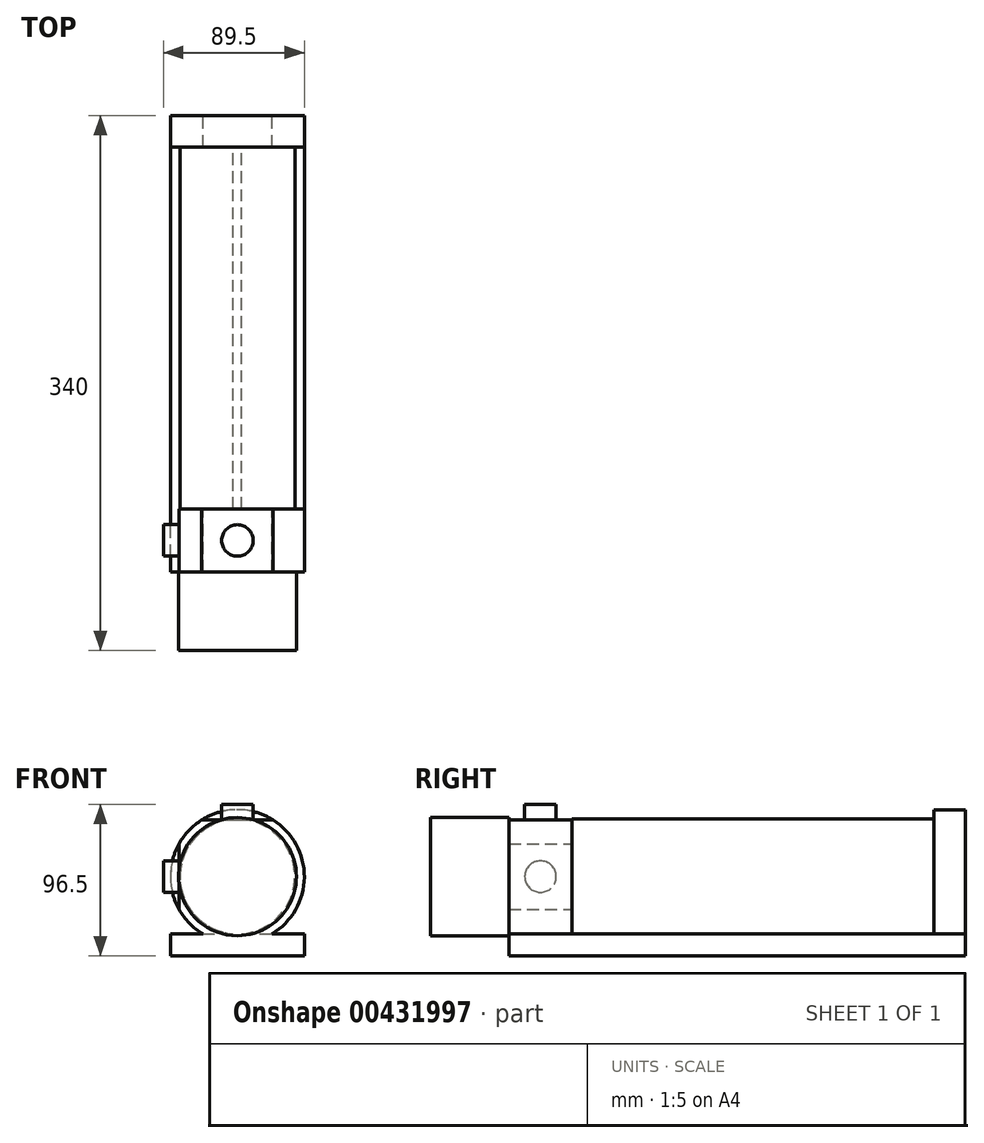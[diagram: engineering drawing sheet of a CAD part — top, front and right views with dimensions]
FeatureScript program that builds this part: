
annotation { "Feature Type Name" : "Feature", "Feature Type Description" : "" }
export const myFeature = defineFeature(function(context is Context, id is Id, definition is map)
    precondition{}
    {
        {
            var Q0;
            Q0=qCreatedBy(makeId("Front.planeOp"),FACE);
            var sketch = newSketch(context, id + "F0", { "sketchPlane" : qUnion([Q0])});
            skCircle(sketch, "E0", {"center": v(0, 0) * mm, "radius": 36.5 * mm});
            skSolve(sketch);
        }
        {
            var Q0;
            Q0=qSketchRegion(id+"F0",true);
            extrude(context, id + "F1", {"entities" : qUnion([Q0]), "depth" : 270 * mm});
        }
        {
            var Q0;
            Q0=makeQuery(id+"F1.opExtrude","CAP_FACE",FACE,{"disambiguationData":[OSD([sQuery(id+"F0.wireOp",EDGE,"E0")])],"isStart":false});
            cPlane(context, id + "F2", {"entities" : qUnion([Q0]), "cplaneType" : CPlaneType.OFFSET, "offset" : 10 * mm, "oppositeDirection" : true, "width" : 150 * mm, "height" : 150 * mm});
        }
        {
            var Q0;
            Q0=qCreatedBy(id+"F2.planeOp",FACE);
            var sketch = newSketch(context, id + "F3", { "sketchPlane" : qUnion([Q0])});
            skArc(sketch, "E1", {"start": v(21.77, -36.5) * mm, "mid": v(0, 42.5) * mm, "end": v(-21.77, -36.5) * mm});
            skLineSegment(sketch, "E2.bottom", {"start": v(-42.5, -38.5) * mm, "end": v(42.5, -38.5) * mm});
            skLineSegment(sketch, "E2.top", {"start": v(-42.5, -36.5) * mm, "end": v(-21.77, -36.5) * mm});
            skLineSegment(sketch, "E2.left", {"start": v(-42.5, -38.5) * mm, "end": v(-42.5, -36.5) * mm});
            skLineSegment(sketch, "E2.right", {"start": v(42.5, -38.5) * mm, "end": v(42.5, -36.5) * mm});
            skLineSegment(sketch, "E3", {"start": v(0, 0) * mm, "end": v(0, -36.5) * mm, "construction": true});
            skLineSegment(sketch, "E4.trimOffspring", {"start": v(21.77, -36.5) * mm, "end": v(42.5, -36.5) * mm});
            skSolve(sketch);
        }
        {
            var Q0;
            Q0=qSketchRegion(id+"F3",true);
            extrude(context, id + "F4", {"entities" : qUnion([Q0]), "operationType" : NewBodyOperationType.ADD, "depth" : 30 * mm, "hasSecondDirection" : true, "secondDirectionOppositeDirection" : true, "secondDirectionDepth" : 10 * mm});
        }
        {
            var Q0;
            Q0=qCreatedBy(makeId("Front.planeOp"),FACE);
            cPlane(context, id + "F5", {"entities" : qUnion([Q0]), "cplaneType" : CPlaneType.OFFSET, "offset" : 10 * mm, "width" : 150 * mm, "height" : 150 * mm});
        }
        {
            var Q0;
            Q0=qCreatedBy(id+"F5.planeOp",FACE);
            var sketch = newSketch(context, id + "F6", { "sketchPlane" : qUnion([Q0])});
            skArc(sketch, "E5.0", {"start": v(21.77, -36.5) * mm, "mid": v(0, 42.5) * mm, "end": v(-21.77, -36.5) * mm});
            skLineSegment(sketch, "E5.1", {"start": v(21.77, -36.5) * mm, "end": v(42.5, -36.5) * mm});
            skLineSegment(sketch, "E5.2", {"start": v(-42.5, -38.5) * mm, "end": v(42.5, -38.5) * mm});
            skLineSegment(sketch, "E5.3", {"start": v(-42.5, -36.5) * mm, "end": v(-21.77, -36.5) * mm});
            skLineSegment(sketch, "E5.4", {"start": v(-42.5, -38.5) * mm, "end": v(-42.5, -36.5) * mm});
            skLineSegment(sketch, "E5.5", {"start": v(42.5, -38.5) * mm, "end": v(42.5, -36.5) * mm});
            skSolve(sketch);
        }
        {
            var Q0;
            Q0=qSketchRegion(id+"F6",true);
            extrude(context, id + "F7", {"entities" : qUnion([Q0]), "operationType" : NewBodyOperationType.ADD, "depth" : 10 * mm, "hasSecondDirection" : true, "secondDirectionOppositeDirection" : true, "secondDirectionDepth" : 10 * mm});
        }
        {
            var Q0;
            Q0=makeQuery(id+"F4.opExtrude","CAP_FACE",FACE,{"disambiguationData":[OSD([sQuery(id+"F3.wireOp",EDGE,"L33eIDpH-reCj-vmiZ-9Mvz-sp26GM8VuCSZ"),sQuery(id+"F3.wireOp",EDGE,"E1"),sQuery(id+"F3.wireOp",EDGE,"E2.bottom"),sQuery(id+"F3.wireOp",EDGE,"E2.top"),sQuery(id+"F3.wireOp",EDGE,"E2.left"),sQuery(id+"F3.wireOp",EDGE,"E2.right"),sQuery(id+"F3.wireOp",EDGE,"E4.trimOffspring")])],"isStart":true});
            var sketch = newSketch(context, id + "F8", { "sketchPlane" : qUnion([Q0])});
            skLineSegment(sketch, "E6.bottom", {"start": v(-42.5, -38.5) * mm, "end": v(42.5, -38.5) * mm});
            skLineSegment(sketch, "E6.left", {"start": v(-42.5, -38.5) * mm, "end": v(-42.5, -36.5) * mm});
            skLineSegment(sketch, "E6.right", {"start": v(42.5, -38.5) * mm, "end": v(42.5, -36.5) * mm});
            skLineSegment(sketch, "E7.0", {"start": v(-21.77, -36.5) * mm, "end": v(-42.5, -36.5) * mm});
            skLineSegment(sketch, "E8.0", {"start": v(42.5, -36.5) * mm, "end": v(21.77, -36.5) * mm});
            skLineSegment(sketch, "E9", {"start": v(-21.77, -36.5) * mm, "end": v(0, -37.5) * mm});
            skLineSegment(sketch, "E10", {"start": v(0, -37.5) * mm, "end": v(21.77, -36.5) * mm});
            skSolve(sketch);
        }
        {
            var Q0;
            Q0=qSketchRegion(id+"F8",true);
            extrude(context, id + "F9", {"entities" : qUnion([Q0]), "operationType" : NewBodyOperationType.ADD, "endBound" : BoundingType.UP_TO_NEXT, "depth" : 25 * mm});
        }
        {
            var Q0;
            Q0=makeQuery(id+"F4.boolean.opBoolean","MERGE",FACE,{"derivedFrom":[makeQuery(id+"F1.opExtrude","CAP_FACE",FACE,{"disambiguationData":[OSD([sQuery(id+"F0.wireOp",EDGE,"E0")])],"isStart":false}),makeQuery(id+"F4.opExtrude","CAP_FACE",FACE,{"disambiguationData":[OSD([sQuery(id+"F3.wireOp",EDGE,"L33eIDpH-reCj-vmiZ-9Mvz-sp26GM8VuCSZ"),sQuery(id+"F3.wireOp",EDGE,"E1"),sQuery(id+"F3.wireOp",EDGE,"E2.bottom"),sQuery(id+"F3.wireOp",EDGE,"E2.top"),sQuery(id+"F3.wireOp",EDGE,"E2.left"),sQuery(id+"F3.wireOp",EDGE,"E2.right"),sQuery(id+"F3.wireOp",EDGE,"E4.trimOffspring")])],"isStart":false})]});
            var sketch = newSketch(context, id + "F10", { "sketchPlane" : qUnion([Q0])});
            skCircle(sketch, "E11", {"center": v(0, 0) * mm, "radius": 37.5 * mm});
            skSolve(sketch);
        }
        {
            var Q0;
            Q0=qSketchRegion(id+"F10",true);
            extrude(context, id + "F11", {"entities" : qUnion([Q0]), "operationType" : NewBodyOperationType.ADD, "depth" : 50 * mm});
        }
        {
            var Q0;
            Q0=qCreatedBy(makeId("Top.planeOp"),FACE);
            cPlane(context, id + "F12", {"entities" : qUnion([Q0]), "cplaneType" : CPlaneType.OFFSET, "offset" : 46 * mm, "width" : 150 * mm, "height" : 150 * mm});
        }
        {
            var Q0;
            Q0=qCreatedBy(id+"F12.planeOp",FACE);
            var sketch = newSketch(context, id + "F13", { "sketchPlane" : qUnion([Q0])});
            skLineSegment(sketch, "E12.bottom", {"start": v(-67.77, -250) * mm, "end": v(67.77, -250) * mm});
            skLineSegment(sketch, "E12.top", {"start": v(-67.77, -290) * mm, "end": v(67.77, -290) * mm});
            skLineSegment(sketch, "E12.left", {"start": v(-67.77, -250) * mm, "end": v(-67.77, -290) * mm});
            skLineSegment(sketch, "E12.right", {"start": v(67.77, -250) * mm, "end": v(67.77, -290) * mm});
            skPoint(sketch, "E12.middle", {"position": v(0, -270) * mm});
            skSolve(sketch);
        }
        {
            var Q0;
            Q0=qSketchRegion(id+"F13",true);
            extrude(context, id + "F14", {"entities" : qUnion([Q0]), "operationType" : NewBodyOperationType.REMOVE, "oppositeDirection" : true, "depth" : 10 * mm});
        }
        {
            var Q0;
            Q0=qCreatedBy(makeId("Right.planeOp"),FACE);
            cPlane(context, id + "F15", {"entities" : qUnion([Q0]), "cplaneType" : CPlaneType.OFFSET, "offset" : 52 * mm, "oppositeDirection" : true, "width" : 150 * mm, "height" : 150 * mm});
        }
        {
            var Q0;
            Q0=qCreatedBy(id+"F15.planeOp",FACE);
            var sketch = newSketch(context, id + "F16", { "sketchPlane" : qUnion([Q0])});
            skLineSegment(sketch, "E13.bottom", {"start": v(-290, 58.78) * mm, "end": v(-250, 58.78) * mm});
            skLineSegment(sketch, "E13.top", {"start": v(-290, -58.78) * mm, "end": v(-250, -58.78) * mm});
            skLineSegment(sketch, "E13.left", {"start": v(-290, 58.78) * mm, "end": v(-290, -58.78) * mm});
            skLineSegment(sketch, "E13.right", {"start": v(-250, 58.78) * mm, "end": v(-250, -58.78) * mm});
            skPoint(sketch, "E13.middle", {"position": v(-270, 0) * mm});
            skSolve(sketch);
        }
        {
            var Q0;
            Q0=qSketchRegion(id+"F16",true);
            extrude(context, id + "F17", {"entities" : qUnion([Q0]), "operationType" : NewBodyOperationType.REMOVE, "depth" : 15 * mm});
        }
        {
            var Q0;
            Q0=makeQuery(id+"F14.boolean.opBoolean","COPY",FACE,{"derivedFrom":makeQuery(id+"F14.opExtrude","CAP_FACE",FACE,{"disambiguationData":[OSD([sQuery(id+"F13.wireOp",EDGE,"E12.bottom"),sQuery(id+"F13.wireOp",EDGE,"E12.top"),sQuery(id+"F13.wireOp",EDGE,"E12.left"),sQuery(id+"F13.wireOp",EDGE,"E12.right")])],"isStart":false})});
            var sketch = newSketch(context, id + "F18", { "sketchPlane" : qUnion([Q0])});
            skCircle(sketch, "E14", {"center": v(0, -270) * mm, "radius": 10 * mm});
            skPoint(sketch, "E14.centerSnap0", {"position": v(22.59, -270) * mm});
            skSolve(sketch);
        }
        {
            var Q0;
            Q0=qSketchRegion(id+"F18",true);
            extrude(context, id + "F19", {"entities" : qUnion([Q0]), "operationType" : NewBodyOperationType.ADD, "depth" : 10 * mm});
        }
        {
            var Q0;
            {var subQ5=sQuery(id+"F3.wireOp",EDGE,"E1");var subQ6=sQuery(id+"F16.wireOp",EDGE,"E13.left");Q0=makeQuery(id+"F17.boolean.opBoolean","COPY",FACE,{"disambiguationData":[TD([makeQuery(id+"F4.opExtrude","SWEPT_FACE",FACE,{"disambiguationData":[OSD([subQ5])]})])],"derivedFrom":makeQuery(id+"F17.opExtrude","CAP_FACE",FACE,{"disambiguationData":[OSD([sQuery(id+"F16.wireOp",EDGE,"E13.bottom"),sQuery(id+"F16.wireOp",EDGE,"E13.top"),subQ6,sQuery(id+"F16.wireOp",EDGE,"E13.right")])],"isStart":false})});}
            var sketch = newSketch(context, id + "F20", { "sketchPlane" : qUnion([Q0])});
            skCircle(sketch, "E15", {"center": v(270, 0) * mm, "radius": 10 * mm});
            skPoint(sketch, "E16", {"position": v(270, 20.91) * mm});
            skSolve(sketch);
        }
        {
            var Q0;
            Q0=qSketchRegion(id+"F20",true);
            extrude(context, id + "F21", {"entities" : qUnion([Q0]), "operationType" : NewBodyOperationType.ADD, "depth" : 10 * mm});
        }
        {
            var Q0;
            Q0=makeQuery(id+"F9.boolean.opBoolean","MERGE",FACE,{"derivedFrom":[makeQuery(id+"F4.opExtrude","SWEPT_FACE",FACE,{"disambiguationData":[OSD([sQuery(id+"F3.wireOp",EDGE,"E2.bottom")])]}),makeQuery(id+"F7.opExtrude","SWEPT_FACE",FACE,{"disambiguationData":[OSD([sQuery(id+"F6.wireOp",EDGE,"E5.2")])]}),makeQuery(id+"F9.opExtrude","SWEPT_FACE",FACE,{"disambiguationData":[OSD([sQuery(id+"F8.wireOp",EDGE,"E6.bottom")])]})]});
            var sketch = newSketch(context, id + "F22", { "sketchPlane" : qUnion([Q0])});
            skLineSegment(sketch, "E17.bottom", {"start": v(42.5, 290) * mm, "end": v(-42.5, 290) * mm});
            skLineSegment(sketch, "E17.top", {"start": v(42.5, 0) * mm, "end": v(-42.5, 0) * mm});
            skLineSegment(sketch, "E17.left", {"start": v(42.5, 290) * mm, "end": v(42.5, 0) * mm});
            skLineSegment(sketch, "E17.right", {"start": v(-42.5, 290) * mm, "end": v(-42.5, 0) * mm});
            skPoint(sketch, "E17.middle", {"position": v(0, 145) * mm});
            skPoint(sketch, "E17.middle.positionSnap0", {"position": v(42.5, 145) * mm});
            skPoint(sketch, "E17.centerSnap0", {"position": v(42.5, 145) * mm});
            skSolve(sketch);
        }
        {
            var Q0;
            Q0=qSketchRegion(id+"F22",true);
            extrude(context, id + "F23", {"entities" : qUnion([Q0]), "operationType" : NewBodyOperationType.ADD, "depth" : 12 * mm, "hasSecondDirection" : true, "secondDirectionOppositeDirection" : true, "secondDirectionDepth" : 2.1 * mm, "offsetDistance" : 25 * mm});
        }
    });
